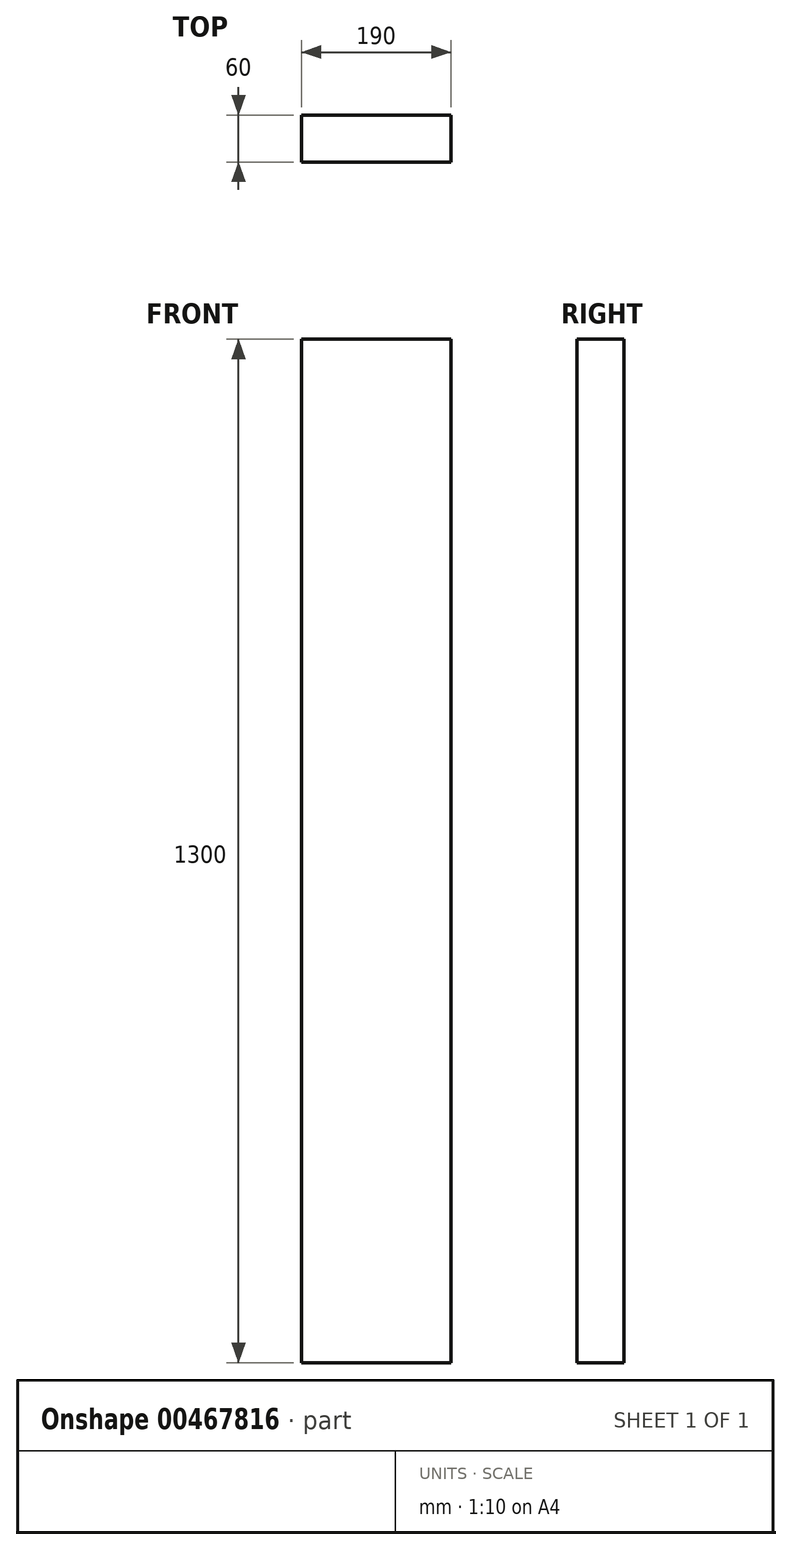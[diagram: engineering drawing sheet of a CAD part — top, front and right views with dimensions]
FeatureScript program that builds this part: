
annotation { "Feature Type Name" : "Feature", "Feature Type Description" : "" }
export const myFeature = defineFeature(function(context is Context, id is Id, definition is map)
    precondition{}
    {
        {
            var Q0;
            Q0=qCreatedBy(makeId("Front.planeOp"),FACE);
            var sketch = newSketch(context, id + "F0", { "sketchPlane" : qUnion([Q0])});
            skLineSegment(sketch, "E0.bottom", {"start": v(190, -3924.72) * mm, "end": v(0, -3924.72) * mm});
            skLineSegment(sketch, "E0.top", {"start": v(190, -5224.72) * mm, "end": v(0, -5224.72) * mm});
            skLineSegment(sketch, "E0.left", {"start": v(190, -3924.72) * mm, "end": v(190, -5224.72) * mm});
            skLineSegment(sketch, "E0.right", {"start": v(0, -3924.72) * mm, "end": v(0, -5224.72) * mm});
            skSolve(sketch);
        }
        {
            var Q0;
            Q0=makeQuery(id+"F0.imprint","IMPRINT",FACE,{"disambiguationData":[TD([[makeQuery(id+"F0.imprint","IMPRINT",EDGE,{"derivedFrom":sQuery(id+"F0.wireOp",EDGE,"E0.bottom")}),1.0]])]});
            extrude(context, id + "F1", {"entities" : qUnion([Q0]), "depth" : 60 * mm});
        }
    });
